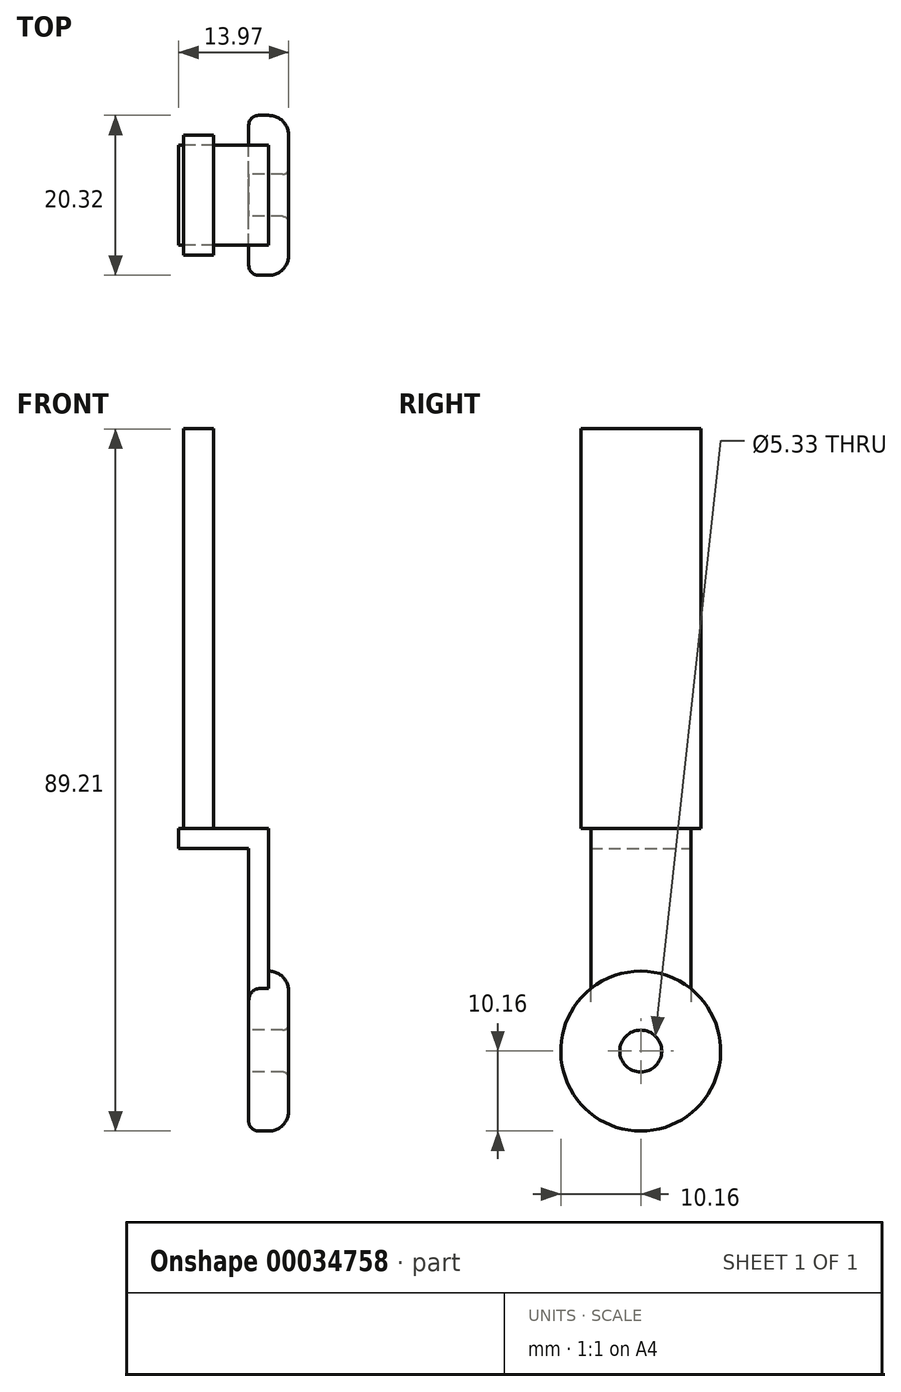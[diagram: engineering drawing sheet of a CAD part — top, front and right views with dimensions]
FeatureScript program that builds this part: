
annotation { "Feature Type Name" : "Feature", "Feature Type Description" : "" }
export const myFeature = defineFeature(function(context is Context, id is Id, definition is map)
    precondition{}
    {
        {
            var Q0;
            Q0=qCreatedBy(makeId("Right.planeOp"),FACE);
            var sketch = newSketch(context, id + "F0", { "sketchPlane" : qUnion([Q0])});
            skCircle(sketch, "E0", {"center": v(0, 0) * mm, "radius": 10.16 * mm});
            skSolve(sketch);
        }
        {
            var Q0;
            Q0 = qSketchRegion(id + "F0", true);
            extrude(context, id + "F1", {"entities" : qUnion([Q0]), "oppositeDirection" : true, "depth" : 2.54 * mm});
        }
        {
            var Q0;
            Q0=makeQuery(id+"F1.opExtrude","CAP_FACE",FACE,{"disambiguationData":[OSD([sQuery(id+"F0.wireOp",EDGE,"E0")])],"isStart":false});
            var sketch = newSketch(context, id + "F2", { "sketchPlane" : qUnion([Q0])});
            skCircle(sketch, "E1", {"center": v(0, 0) * mm, "radius": 2.67 * mm});
            skSolve(sketch);
        }
        {
            var Q0;
            Q0 = qSketchRegion(id + "F2", true);
            extrude(context, id + "F3", {"entities" : qUnion([Q0]), "operationType" : NewBodyOperationType.REMOVE, "oppositeDirection" : true, "depth" : 26.02 * mm});
        }
        {
            var Q0;
            Q0=qCreatedBy(makeId("Right.planeOp"),FACE);
            var sketch = newSketch(context, id + "F4", { "sketchPlane" : qUnion([Q0])});
            skCircle(sketch, "E2", {"center": v(0, 0) * mm, "radius": 10.16 * mm});
            skSolve(sketch);
        }
        {
            var Q0;
            Q0 = qSketchRegion(id + "F4", true);
            extrude(context, id + "F5", {"entities" : qUnion([Q0]), "operationType" : NewBodyOperationType.ADD, "oppositeDirection" : true, "depth" : 5.08 * mm});
        }
        {
            var Q0;
            Q0=makeQuery(id+"F5.opExtrude","CAP_FACE",FACE,{"disambiguationData":[OSD([sQuery(id+"F4.wireOp",EDGE,"E2")])],"isStart":false});
            var sketch = newSketch(context, id + "F6", { "sketchPlane" : qUnion([Q0])});
            skLineSegment(sketch, "E3", {"start": v(-6.35, 7.93) * mm, "end": v(6.35, 7.93) * mm});
            skLineSegment(sketch, "E4", {"start": v(6.35, 7.93) * mm, "end": v(6.35, 28.25) * mm});
            skLineSegment(sketch, "E5", {"start": v(6.35, 28.25) * mm, "end": v(-6.35, 28.25) * mm});
            skLineSegment(sketch, "E6", {"start": v(-6.35, 28.25) * mm, "end": v(-6.35, 7.93) * mm});
            skSolve(sketch);
        }
        {
            var Q0;
            {var subQ1=sQuery(id+"F6.wireOp",EDGE,"E3");Q0=makeQuery(id+"F6.imprint","IMPRINT",FACE,{"disambiguationData":[TD([[makeQuery(id+"F6.imprint","IMPRINT",EDGE,{"derivedFrom":subQ1}),-1.0]])]});}
            var sketch = newSketch(context, id + "F7", { "sketchPlane" : qUnion([Q0])});
            skCircle(sketch, "E7", {"center": v(0, 0) * mm, "radius": 2.67 * mm});
            skSolve(sketch);
        }
        {
            var Q0;
            Q0 = qSketchRegion(id + "F7", true);
            extrude(context, id + "F8", {"entities" : qUnion([Q0]), "operationType" : NewBodyOperationType.REMOVE, "oppositeDirection" : true, "depth" : 61.3 * mm});
        }
        {
            var Q0;
            {var subQ3=sQuery(id+"F6.wireOp",EDGE,"E4");Q0=makeQuery(id+"F6.imprint","IMPRINT",FACE,{"disambiguationData":[TD([[makeQuery(id+"F6.imprint","IMPRINT",EDGE,{"derivedFrom":subQ3}),1.0]])]});}
            extrude(context, id + "F9", {"entities" : qUnion([Q0]), "operationType" : NewBodyOperationType.ADD, "oppositeDirection" : true, "depth" : 2.54 * mm});
        }
        {
            var Q0;
            Q0=makeQuery(id+"F9.opExtrude","SWEPT_FACE",FACE,{"disambiguationData":[OSD([sQuery(id+"F6.wireOp",EDGE,"E5")])]});
            var sketch = newSketch(context, id + "F10", { "sketchPlane" : qUnion([Q0])});
            skLineSegment(sketch, "E8", {"start": v(-5.08, 6.35) * mm, "end": v(-13.97, 6.35) * mm});
            skLineSegment(sketch, "E9", {"start": v(-13.97, 6.35) * mm, "end": v(-13.97, -6.35) * mm});
            skLineSegment(sketch, "E10", {"start": v(-13.97, -6.35) * mm, "end": v(-5.08, -6.35) * mm});
            skSolve(sketch);
        }
        {
            var Q0;
            Q0 = qSketchRegion(id + "F10", true);
            var Q1;
            Q1=makeQuery(id+"F10.imprint","IMPRINT",FACE,{"disambiguationData":[TD([[makeQuery(id+"F10.imprint","IMPRINT",EDGE,{"derivedFrom":sQuery(id+"F10.wireOp",EDGE,"E8")}),1.0]])]});
            extrude(context, id + "F11", {"entities" : qUnion([Q0, Q1]), "operationType" : NewBodyOperationType.ADD, "oppositeDirection" : true, "depth" : 2.54 * mm});
        }
        {
            var Q0;
            {var subQ0=sQuery(id+"F6.wireOp",EDGE,"E5");Q0=makeQuery(id+"F11.boolean.opBoolean","MERGE",FACE,{"derivedFrom":[makeQuery(id+"F9.opExtrude","SWEPT_FACE",FACE,{"disambiguationData":[OSD([subQ0])]}),makeQuery(id+"F11.opExtrude","CAP_FACE",FACE,{"disambiguationData":[OSD([subQ0,sQuery(id+"F10.wireOp",EDGE,"E8"),sQuery(id+"F10.wireOp",EDGE,"E9"),sQuery(id+"F10.wireOp",EDGE,"E10")])],"isStart":true})]});}
            var sketch = newSketch(context, id + "F12", { "sketchPlane" : qUnion([Q0])});
            skLineSegment(sketch, "E11", {"start": v(-13.34, 7.62) * mm, "end": v(-9.55, 7.62) * mm});
            skLineSegment(sketch, "E12", {"start": v(-9.55, 7.62) * mm, "end": v(-9.55, -7.62) * mm});
            skLineSegment(sketch, "E13", {"start": v(-9.55, -7.62) * mm, "end": v(-13.33, -7.62) * mm});
            skLineSegment(sketch, "E14", {"start": v(-13.34, -7.62) * mm, "end": v(-13.34, 7.62) * mm});
            skLineSegment(sketch, "E15", {"start": v(-9.55, 7.62) * mm, "end": v(-9.55, 0) * mm});
            skSolve(sketch);
        }
        {
            var Q0;
            Q0 = qSketchRegion(id + "F12", true);
            extrude(context, id + "F13", {"entities" : qUnion([Q0]), "operationType" : NewBodyOperationType.ADD, "depth" : 50.8 * mm});
        }
        {
            var Q0;
            Q0=makeQuery(id+"F1.opExtrude","CAP_EDGE",EDGE,{"disambiguationData":[OSD([sQuery(id+"F0.wireOp",EDGE,"E0")])],"isStart":true});
            fillet(context, id + "F14", {"entities" : qUnion([Q0]), "radius" : 2.54 * mm, "tangentPropagation" : true, "allowEdgeOverflow" : false});
        }
        {
            var Q0;
            Q0=makeQuery(id+"F5.opExtrude","CAP_EDGE",EDGE,{"disambiguationData":[OSD([sQuery(id+"F4.wireOp",EDGE,"E2")])],"isStart":false});
            fillet(context, id + "F15", {"entities" : qUnion([Q0]), "radius" : 1.27 * mm, "tangentPropagation" : true, "allowEdgeOverflow" : false});
        }
        {
            var Q0;
            Q0=makeQuery(id+"F8.boolean.opBoolean","COPY",EDGE,{"derivedFrom":makeQuery(id+"F8.opExtrude","CAP_EDGE",EDGE,{"disambiguationData":[OSD([sQuery(id+"F7.wireOp",EDGE,"E7")])],"isStart":true})});
            var Q1;
            Q1=makeQuery(id+"F8.boolean.opBoolean","INTERSECT",EDGE,{"derivedFrom":[makeQuery(id+"F5.boolean.opBoolean","MERGE",FACE,{"derivedFrom":[makeQuery(id+"F1.opExtrude","CAP_FACE",FACE,{"disambiguationData":[OSD([sQuery(id+"F0.wireOp",EDGE,"E0")])],"isStart":true}),makeQuery(id+"F5.opExtrude","CAP_FACE",FACE,{"disambiguationData":[OSD([sQuery(id+"F4.wireOp",EDGE,"E2")])],"isStart":true})]}),makeQuery(id+"F8.opExtrude","SWEPT_FACE",FACE,{"disambiguationData":[OSD([sQuery(id+"F7.wireOp",EDGE,"E7")])]})]});
            fillet(context, id + "F16", {"entities" : qUnion([Q0, Q1]), "radius" : 0.76 * mm, "tangentPropagation" : true, "allowEdgeOverflow" : false});
        }
    });
